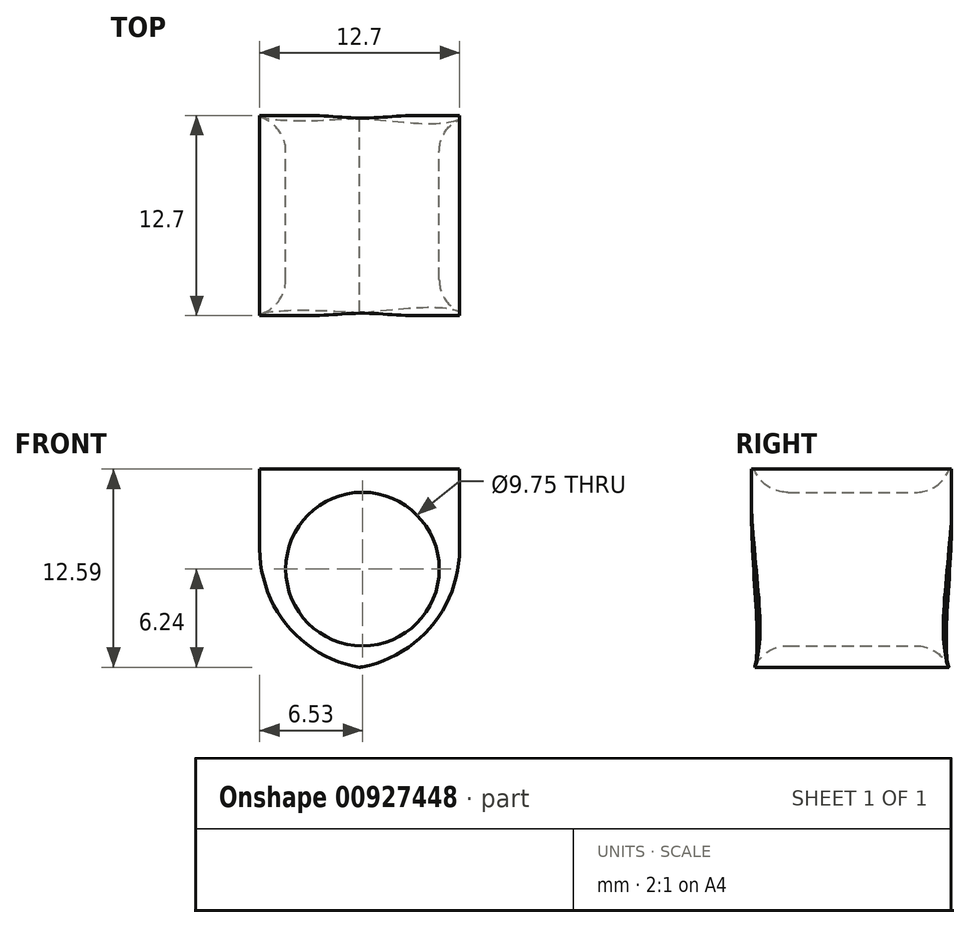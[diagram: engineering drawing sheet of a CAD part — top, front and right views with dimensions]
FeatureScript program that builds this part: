
annotation { "Feature Type Name" : "Feature", "Feature Type Description" : "" }
export const myFeature = defineFeature(function(context is Context, id is Id, definition is map)
    precondition{}
    {
        {
            var Q0;
            Q0=qCreatedBy(makeId("Front.planeOp"),FACE);
            var sketch = newSketch(context, id + "F0", { "sketchPlane" : qUnion([Q0])});
            skLineSegment(sketch, "E0", {"start": v(-6.53, 9.34) * mm, "end": v(-6.53, -3.36) * mm});
            skLineSegment(sketch, "E1", {"start": v(-6.53, -3.36) * mm, "end": v(6.17, -3.36) * mm});
            skLineSegment(sketch, "E2", {"start": v(6.17, 9.34) * mm, "end": v(-6.53, 9.34) * mm});
            skLineSegment(sketch, "E3", {"start": v(6.17, -3.36) * mm, "end": v(6.17, 9.34) * mm});
            skCircle(sketch, "E4", {"center": v(0, 3) * mm, "radius": 4.87 * mm});
            skPoint(sketch, "E4.centerSnap0", {"position": v(6.17, 3) * mm});
            skSolve(sketch);
        }
        {
            var Q0;
            Q0 = qSketchRegion(id + "F0", true);
            extrude(context, id + "F1", {"entities" : qUnion([Q0]), "depth" : 12.7 * mm, "offsetDistance" : 25.4 * mm});
        }
        {
            var Q0;
            Q0=makeQuery(id+"F1.opExtrude","CAP_EDGE",EDGE,{"disambiguationData":[OSD([sQuery(id+"F0.wireOp",EDGE,"E4")])],"isStart":false});
            var Q1;
            Q1=makeQuery(id+"F1.opExtrude","CAP_EDGE",EDGE,{"disambiguationData":[OSD([sQuery(id+"F0.wireOp",EDGE,"E4")])],"isStart":true});
            fillet(context, id + "F2", {"entities" : qUnion([Q0, Q1]), "radius" : 2.3 * mm, "tangentPropagation" : true, "allowEdgeOverflow" : false});
        }
        {
            var Q0;
            Q0=makeQuery(id+"F1.opExtrude","SWEPT_EDGE",EDGE,{"disambiguationData":[OSD([sQuery(id+"F0.wireOp",EDGE,"E1"),sQuery(id+"F0.wireOp",EDGE,"E3")])]});
            var Q1;
            Q1=makeQuery(id+"F1.opExtrude","SWEPT_EDGE",EDGE,{"disambiguationData":[OSD([sQuery(id+"F0.wireOp",EDGE,"E0"),sQuery(id+"F0.wireOp",EDGE,"E1")])]});
            fillet(context, id + "F3", {"entities" : qUnion([Q0, Q1]), "radius" : 7.62 * mm, "tangentPropagation" : true, "allowEdgeOverflow" : false});
        }
    });
